FCSTD DOCUMENT  (FreeCAD 1.0R38641 +678 (Git))
Label: Disco_assembly
License: All rights reserved
LicenseURL: https://en.wikipedia.org/wiki/All_rights_reserved
objects: App::Link×6, App::FeaturePython×5, Assembly::JointGroup×1, Assembly::AssemblyObject×1
EXTERNAL_REF file=Disco_base.FCStd obj=Body
EXTERNAL_REF file=Disco_base.FCStd obj=Body001
EXTERNAL_REF file=Disco_deck.FCStd obj=Body001
EXTERNAL_REF file=Disco_motor-spool.FCStd obj=Body
EXTERNAL_REF file=Disco_ball.FCStd obj=Body

FEATURE [App::Link] ColorLEDdeck
  LinkedObject = -> <external Disco_base.FCStd>#Body
FEATURE [App::FeaturePython] GroundedJoint  # Assembly grounded joint (typed FeaturePython)
  ObjectToGround = -> ColorLEDdeck
FEATURE [App::Link] Body
  LinkPlacement = pos=(-5e-16,0,0) rot=(0,0,1;0rad)
  LinkedObject = -> <external Disco_base.FCStd>#Body001
  Placement = pos=(-5e-16,0,0) rot=(0,0,1;0rad)
FEATURE [App::Link] Body001
  LinkPlacement = pos=(0,0,0) rot=(0,0,1;3.14159rad)
  LinkedObject = -> <external Disco_base.FCStd>#Body001
  Placement = pos=(0,0,0) rot=(0,0,1;3.14159rad)
FEATURE [App::Link] Body002
  LinkPlacement = pos=(-0.0296618,0.020308,-2.57969) rot=(0.57735,0.57735,-0.57735;2.0944rad)
  LinkedObject = -> <external Disco_deck.FCStd>#Body001
  Placement = pos=(-0.0296618,0.020308,-2.57969) rot=(0.57735,0.57735,-0.57735;2.0944rad)
FEATURE [App::Link] Body003
  LinkPlacement = pos=(-0.0413632,-24.6067,1.66004) rot=(0,0,1;0rad)
  LinkedObject = -> <external Disco_motor-spool.FCStd>#Body
  Placement = pos=(-0.0413632,-24.6067,1.66004) rot=(0,0,1;0rad)
FEATURE [App::Link] Body004
  LinkPlacement = pos=(-1.4e-15,-1.316e-13,8.9e-15) rot=(0,0,1;3.14159rad)
  LinkedObject = -> <external Disco_ball.FCStd>#Body
  Placement = pos=(-1.4e-15,-1.316e-13,8.9e-15) rot=(0,0,1;3.14159rad)
FEATURE [App::FeaturePython] Joint  label="Distance"  # Assembly joint (typed FeaturePython)
  Activated = true
  AngleMax = 0
  AngleMin = 0
  Detach1 = false
  Detach2 = false
  Distance = 0
  Distance2 = 0
  EnableAngleMax = false
  EnableAngleMin = false
  EnableLengthMax = false
  EnableLengthMin = false
  JointType = 5 (Distance)
  LengthMax = 0
  LengthMin = 0
  Placement1 = pos=(-14.2217,-1.5e-15,0) rot=(0,1,0;3.14159rad)
  Placement2 = pos=(-1.1e-15,-1.43e-13,0) rot=(0,0,1;0rad)
  Reference1 = -> Assembly [Body.Hole.Face2,Body.Hole.Face2]
  Reference2 = -> Assembly [ColorLEDdeck.Pad.Face11,ColorLEDdeck.Pad.Face11]
FEATURE [App::FeaturePython] Joint001  label="Fixed"  # Assembly joint (typed FeaturePython)
  Activated = true
  AngleMax = 0
  AngleMin = 0
  Detach1 = false
  Detach2 = false
  Distance = 0
  Distance2 = 0
  EnableAngleMax = false
  EnableAngleMin = false
  EnableLengthMax = false
  EnableLengthMin = false
  JointType = 0 (Fixed)
  LengthMax = 0
  LengthMin = 0
  Placement1 = pos=(-15,0,0) rot=(0,1,0;3.14159rad)
  Placement2 = pos=(-15,0,0) rot=(0,0,1;0rad)
  Reference1 = -> Assembly [Body.Hole.Edge14,Body.Hole.Edge14]
  Reference2 = -> Assembly [ColorLEDdeck.Pad.Edge29,ColorLEDdeck.Pad.Edge29]
FEATURE [App::FeaturePython] Joint002  label="Fixed001"  # Assembly joint (typed FeaturePython)
  Activated = true
  AngleMax = 0
  AngleMin = 0
  Detach1 = false
  Detach2 = false
  Distance = 0
  Distance2 = 0
  EnableAngleMax = false
  EnableAngleMin = false
  EnableLengthMax = false
  EnableLengthMin = false
  JointType = 0 (Fixed)
  LengthMax = 0
  LengthMin = 0
  Placement1 = pos=(-15,0,0) rot=(0,-1,0;3.14159rad)
  Placement2 = pos=(15,0,0) rot=(0,0,1;0rad)
  Reference1 = -> Assembly [Body001.Hole.Edge14,Body001.Hole.Edge14]
  Reference2 = -> Assembly [ColorLEDdeck.Pad.Edge26,ColorLEDdeck.Pad.Edge26]
FEATURE [App::FeaturePython] Joint003  label="Distance001"  # Assembly joint (typed FeaturePython)
  Activated = true
  AngleMax = 0
  AngleMin = 0
  Detach1 = false
  Detach2 = false
  Distance = 0
  Distance2 = 0
  EnableAngleMax = false
  EnableAngleMin = false
  EnableLengthMax = false
  EnableLengthMin = false
  JointType = 5 (Distance)
  LengthMax = 0
  LengthMin = 0
  Placement1 = pos=(9.4e-15,1.08e-14,-8.9e-15) rot=(0,0,-1;3.14159rad)
  Placement2 = pos=(-1.1e-15,-1.43e-13,0) rot=(0,0,1;0rad)
  Reference1 = -> Assembly [Body004.Cylinder003.Face33,Body004.Cylinder003.Face33]
  Reference2 = -> Assembly [ColorLEDdeck.Pad.Face11,ColorLEDdeck.Pad.Face11]
FEATURE [Assembly::JointGroup] Joints
  Group = -> [GroundedJoint,Joint,Joint001,Joint002,Joint003]
FEATURE [Assembly::AssemblyObject] Assembly
  Group = -> [Joints,ColorLEDdeck,GroundedJoint,Body,Body001,Body002,Body003,Body004,Joint,Joint001,Joint002,Joint003]
  Origin = -> Origin
  Type = Assembly

RESOLVED EXTERNAL PARTS (link-assembly join: the EXTERNAL_REF files above that resolve inside this repo's crawl, each included once):
---- part Disco_ball.FCStd = doc fcstd_ed00773c9699 ----
FCSTD DOCUMENT  (FreeCAD 1.0R38641 +678 (Git))
Label: Disco_ball
License: All rights reserved
LicenseURL: https://en.wikipedia.org/wiki/All_rights_reserved
objects: PartDesign::PolarPattern×4, PartDesign::SubtractiveCylinder×4, Sketcher::SketchObject×2, PartDesign::Revolution×1, PartDesign::Plane×1, PartDesign::Pocket×1, PartDesign::Body×1
note: 32 computed .brp shape members not serialized (recipe doc carries the construction recipe); baked Part::Feature solids carry a one-line shape summary decoded from their .brp

FEATURE [Sketcher::SketchObject] Sketch
  ArcFitTolerance = 1e-06
  AttachmentSupport = -> [XZ_Plane]
  FullyConstrained = true
  MakeInternals = false
  MapMode = 5
  Placement = pos=(0,0,0) rot=(1,0,0;1.5708rad)
  sketch-geometry (15):
    g0: LineSegment [constr] StartX=-16.6 StartY=0 StartZ=0 EndX=-16.6 EndY=-0.8 EndZ=0
    g1: LineSegment [constr] StartX=-16.6 StartY=-0.8 StartZ=0 EndX=16.6 EndY=-0.8 EndZ=0
    g2: LineSegment [constr] StartX=16.6 StartY=-0.8 StartZ=0 EndX=16.6 EndY=0 EndZ=0
    g3: LineSegment [constr] StartX=16.6 StartY=0 StartZ=0 EndX=-16.6 EndY=0 EndZ=0
    g4: ArcOfCircle CenterX=0 CenterY=15 CenterZ=0 NormalX=0 NormalY=0 NormalZ=1 AngleXU=0 Radius=16 StartAngle=5.3481 EndAngle=7.85398
    g5: ArcOfCircle CenterX=0 CenterY=15 CenterZ=0 NormalX=0 NormalY=0 NormalZ=1 AngleXU=0 Radius=17 StartAngle=5.54023 EndAngle=7.85398
    g6: LineSegment StartX=0 StartY=32 StartZ=0 EndX=4.9e-15 EndY=31 EndZ=0
    g7: LineSegment StartX=11.7 StartY=1.45 StartZ=0 EndX=13.5 EndY=1.45 EndZ=0
    g8: LineSegment StartX=9.5 StartY=2.12561 StartZ=0 EndX=9.5 EndY=0 EndZ=0
    g9: LineSegment StartX=9.5 StartY=0 StartZ=0 EndX=13.5 EndY=0 EndZ=0
    g10: LineSegment StartX=13.5 StartY=0 StartZ=0 EndX=13.5 EndY=1.45 EndZ=0
    g11: ArcOfCircle CenterX=11.7 CenterY=1.75 CenterZ=0 NormalX=0 NormalY=0 NormalZ=1 AngleXU=0 Radius=0.3 StartAngle=2.08659 EndAngle=4.71239
    g12: LineSegment StartX=12.52 StartY=3.5 StartZ=0 EndX=13.42 EndY=3.5 EndZ=0
    g13: LineSegment StartX=11.552 StartY=2.01097 StartZ=0 EndX=13.5186 EndY=3.12602 EndZ=0
    g14: ArcOfCircle CenterX=13.42 CenterY=3.3 CenterZ=0 NormalX=0 NormalY=0 NormalZ=1 AngleXU=0 Radius=0.2 StartAngle=5.22819 EndAngle=7.85398
  constraints (43):
    c: Coincident(g0,g1)
    c: Coincident(g1,g2)
    c: Coincident(g2,g3)
    c: Coincident(g3,g0)
    c: Vertical(g0)
    c: Vertical(g2)
    c: Horizontal(g1)
    c: Symmetric(g2,g0,g-2)
    c: PointOnObject(g0,g-1)
    c: Distance(g1,g1) = 33.2
    c: Distance(g0,g0) = 0.8
    c: PointOnObject(g4,g-2)
    c: Diameter(g4) = 32
    c: DistanceY(g-1,g4) = 15
    c: PointOnObject(g4,g-2)
    c: Coincident(g5,g4)
    c: PointOnObject(g5,g-2)
    c: Coincident(g6,g5)
    c: Coincident(g6,g4)
    c: Horizontal(g7)
    c: Distance(g9,g7) = 1.45
    c: Coincident(g8,g4)
    c: PointOnObject(g8,g3)
    c: Coincident(g9,g8)
    c: Vertical(g8)
    c: Coincident(g10,g9)
    c: Coincident(g10,g7)
    c: Vertical(g10)
    c: PointOnObject(g9,g-1)
    c: DistanceX(g-1,g9) = 13.5
    c: Diameter(g11) = 0.6
    c: Distance(g4,g5) = 1
    c: Tangent(g11,g7) = -1.5708
    c: DistanceX(g9,g9) = 4
    c: Horizontal(g12)
    c: Coincident(g5,g12)
    c: Tangent(g13,g11) = 1.5708
    c: DistanceX(g7,g7) = 1.8
    c: Diameter(g14) = 0.4
    c: Distance(g12,g12) = 0.9
    c: DistanceY(g-1,g12) = 3.5
    c: Tangent(g14,g12) = 1.5708
    c: Tangent(g14,g13) = -1.5708
FEATURE [PartDesign::Revolution] Revolution
  Angle = 360
  Angle2 = 60
  Axis = (0,2e-16,1)
  Base = (0,0,0)
  Placement = pos=(0,0,0) rot=(1,0,0;1.5708rad)
  Profile = -> Sketch
  ReferenceAxis = -> Sketch [V_Axis]
  Refine = true
  Reversed = true
  Suppressed = false
  Type = 0
FEATURE [PartDesign::Plane] DatumPlane
  AttachmentOffset = pos=(19,0,0) rot=(0,1,0;1.5708rad)
  AttachmentSupport = -> [Revolution]
  Length = 60
  MapMode = 45
  Placement = pos=(19,4.9e-15,17.75) rot=(0,1,0;1.5708rad)
  ResizeMode = 0
  Width = 60
FEATURE [Sketcher::SketchObject] Sketch001
  ArcFitTolerance = 1e-06
  AttachmentSupport = -> [DatumPlane]
  FullyConstrained = true
  MakeInternals = false
  MapMode = 5
  Placement = pos=(19,4.9e-15,17.75) rot=(0,1,0;1.5708rad)
  sketch-geometry (1):
    g0: Circle CenterX=0 CenterY=0 CenterZ=0 NormalX=0 NormalY=0 NormalZ=1 AngleXU=0 Radius=3
  constraints (2):
    c: Coincident(g0,g-1)
    c: Diameter(g0) = 6
FEATURE [PartDesign::Pocket] Pocket
  BaseFeature = -> Revolution
  Direction = (-1,0,-2e-16)
  Length = 7
  Length2 = 5
  Placement = pos=(0,0,0) rot=(1,0,0;1.5708rad)
  Profile = -> Sketch001
  ReferenceAxis = -> Sketch001 [N_Axis]
  Refine = true
  Suppressed = false
  Type = 0
FEATURE [PartDesign::PolarPattern] PolarPattern
  Angle = 360
  Axis = -> Z_Axis
  BaseFeature = -> Pocket
  Mode = 0
  Occurrences = 8
  Offset = 120
  Originals = -> [Pocket]
  Placement = pos=(0,0,0) rot=(1,0,0;1.5708rad)
  Refine = true
  Suppressed = false
  TransformMode = 0
FEATURE [PartDesign::SubtractiveCylinder] Cylinder
  Angle = 360
  AttacherType = Attacher::AttachEngine3D
  AttachmentOffset = pos=(0,17.7,0) rot=(-0.799605,-0.580063,-0.155428;0.646683rad)
  AttachmentSupport = -> [YZ_Plane]
  BaseFeature = -> PolarPattern
  FirstAngle = 0
  Height = 21
  MapMode = 5
  Placement = pos=(0,0,17.7) rot=(0.595507,0.401675,0.695721;1.53984rad)
  Radius = 3
  Refine = true
  SecondAngle = 0
  Suppressed = false
FEATURE [PartDesign::PolarPattern] PolarPattern001
  Angle = 360
  Axis = -> Z_Axis
  BaseFeature = -> Cylinder
  Mode = 0
  Occurrences = 8
  Offset = 120
  Originals = -> [Cylinder]
  Placement = pos=(0,0,17.7) rot=(0.595507,0.401675,0.695721;1.53984rad)
  Refine = true
  Suppressed = false
  TransformMode = 0
FEATURE [PartDesign::SubtractiveCylinder] Cylinder001
  Angle = 360
  AttacherType = Attacher::AttachEngine3D
  AttachmentOffset = pos=(0,17.7,0) rot=(-1,0,0;1.0472rad)
  AttachmentSupport = -> [XZ_Plane]
  BaseFeature = -> PolarPattern001
  FirstAngle = 0
  Height = 25
  MapMode = 5
  Placement = pos=(0,3.9e-15,17.7) rot=(1,0,0;0.523599rad)
  Radius = 3
  Refine = true
  SecondAngle = 0
  Suppressed = false
FEATURE [PartDesign::PolarPattern] PolarPattern002
  Angle = 360
  Axis = -> Z_Axis
  BaseFeature = -> Cylinder001
  Mode = 0
  Occurrences = 4
  Offset = 120
  Originals = -> [Cylinder001]
  Placement = pos=(0,3.9e-15,17.7) rot=(1,0,0;0.523599rad)
  Refine = true
  Suppressed = false
  TransformMode = 0
FEATURE [PartDesign::SubtractiveCylinder] Cylinder002
  Angle = 360
  AttacherType = Attacher::AttachEngine3D
  AttachmentOffset = pos=(0,17.7,0) rot=(0.744004,-0.652337,0.14462;0.579196rad)
  AttachmentSupport = -> [XZ_Plane]
  BaseFeature = -> PolarPattern002
  FirstAngle = 0
  Height = 37
  MapMode = 5
  Placement = pos=(0,3.9e-15,17.7) rot=(0.974454,-0.189415,-0.12067;2.03045rad)
  Radius = 3
  Refine = true
  SecondAngle = 0
  Suppressed = false
FEATURE [PartDesign::PolarPattern] PolarPattern003
  Angle = 360
  Axis = -> Z_Axis
  BaseFeature = -> Cylinder002
  Mode = 0
  Occurrences = 8
  Offset = 120
  Originals = -> [Cylinder002]
  Placement = pos=(0,3.9e-15,17.7) rot=(0.974454,-0.189415,-0.12067;2.03045rad)
  Refine = true
  Suppressed = false
  TransformMode = 0
FEATURE [PartDesign::SubtractiveCylinder] Cylinder003
  Angle = 360
  AttacherType = Attacher::AttachEngine3D
  AttachmentSupport = -> [XY_Plane]
  BaseFeature = -> PolarPattern003
  FirstAngle = 0
  Height = 46
  MapMode = 5
  Radius = 3
  Refine = true
  SecondAngle = 0
  Suppressed = false
FEATURE [PartDesign::Body] Body
  AllowCompound = false
  Group = -> [Sketch,Revolution,DatumPlane,Sketch001,Pocket,PolarPattern,Cylinder,PolarPattern001,Cylinder001,PolarPattern002,Cylinder002,PolarPattern003,Cylinder003]
  Origin = -> Origin
  Tip = -> Cylinder003
---- part Disco_base.FCStd = doc fcstd_412642338aae ----
FCSTD DOCUMENT  (FreeCAD 1.0R38641 +678 (Git))
Label: Disco_base
License: All rights reserved
LicenseURL: https://en.wikipedia.org/wiki/All_rights_reserved
objects: Sketcher::SketchObject×5, PartDesign::Pad×4, PartDesign::Mirrored×3, PartDesign::Body×2, PartDesign::Hole×1
note: 33 computed .brp shape members not serialized (recipe doc carries the construction recipe); baked Part::Feature solids carry a one-line shape summary decoded from their .brp

FEATURE [Sketcher::SketchObject] Sketch
  ArcFitTolerance = 1e-06
  AttachmentSupport = -> [XY_Plane]
  FullyConstrained = true
  MakeInternals = false
  MapMode = 5
  sketch-geometry (10):
    g0: ArcOfCircle CenterX=0 CenterY=0 CenterZ=0 NormalX=0 NormalY=0 NormalZ=1 AngleXU=0 Radius=16.6347 StartAngle=3.37071 EndAngle=4.48327
    g1: LineSegment StartX=-3.77799 StartY=16.2 StartZ=0 EndX=3.77799 EndY=16.2 EndZ=0
    g2: LineSegment StartX=-3.77799 StartY=-16.2 StartZ=0 EndX=3.77799 EndY=-16.2 EndZ=0
    g3: LineSegment StartX=-16.2 StartY=3.77799 StartZ=0 EndX=-16.2 EndY=-3.77799 EndZ=0
    g4: LineSegment StartX=16.2 StartY=3.77799 StartZ=0 EndX=16.2 EndY=-3.77799 EndZ=0
    g5: ArcOfCircle CenterX=0 CenterY=0 CenterZ=0 NormalX=0 NormalY=0 NormalZ=1 AngleXU=0 Radius=16.6347 StartAngle=0.229115 EndAngle=1.34168
    g6: ArcOfCircle CenterX=0 CenterY=0 CenterZ=0 NormalX=0 NormalY=0 NormalZ=1 AngleXU=0 Radius=16.6347 StartAngle=4.9415 EndAngle=6.05407
    g7: ArcOfCircle CenterX=0 CenterY=0 CenterZ=0 NormalX=0 NormalY=0 NormalZ=1 AngleXU=0 Radius=16.6347 StartAngle=1.79991 EndAngle=2.91248
    g8: Circle CenterX=-15 CenterY=0 CenterZ=0 NormalX=0 NormalY=0 NormalZ=1 AngleXU=0 Radius=0.86
    g9: Circle CenterX=15 CenterY=0 CenterZ=0 NormalX=0 NormalY=0 NormalZ=1 AngleXU=0 Radius=0.86
  constraints (32):
    c: Coincident(g0,g-1)
    c: Radius(g0) = 16.6347
    c: PointOnObject(g1,g7)
    c: Horizontal(g1)
    c: PointOnObject(g2,g6)
    c: Horizontal(g2)
    c: Symmetric(g1,g2,g-1)
    c: Distance(g2,g1) = 32.4
    c: Vertical(g3)
    c: PointOnObject(g4,g5)
    c: Vertical(g4)
    c: Symmetric(g3,g4,g-2)
    c: Distance(g4,g3) = 32.4
    c: Coincident(g7,g3)
    c: Coincident(g0,g3)
    c: Equal(g0,g5)
    c: PointOnObject(g6,g4)
    c: PointOnObject(g5,g4)
    c: Coincident(g0,g5)
    c: Equal(g0,g6)
    c: PointOnObject(g0,g2)
    c: PointOnObject(g6,g2)
    c: Coincident(g0,g6)
    c: Equal(g5,g7)
    c: Coincident(g5,g1)
    c: PointOnObject(g7,g1)
    c: Coincident(g5,g7)
    c: PointOnObject(g8,g-1)
    c: Diameter(g8) = 1.72
    c: Diameter(g9) = 1.72
    c: Symmetric(g8,g9,g-2)
    c: DistanceX(g8,g9) = 30
FEATURE [PartDesign::Pad] Pad
  Direction = (0,0,1)
  Length = 0.8
  Length2 = 10
  Profile = -> Sketch
  ReferenceAxis = -> Sketch [N_Axis]
  Refine = true
  Reversed = true
  Suppressed = false
  Type = 0
FEATURE [PartDesign::Body] Body  label="ColorLEDdeck"
  AllowCompound = false
  Group = -> [Sketch,Pad]
  Origin = -> Origin
  Tip = -> Pad
FEATURE [Sketcher::SketchObject] Sketch001
  ArcFitTolerance = 1e-06
  AttachmentSupport = -> [XY_Plane001]
  FullyConstrained = true
  MakeInternals = false
  MapMode = 5
  sketch-geometry (4):
    g0: ArcOfCircle CenterX=0 CenterY=0 CenterZ=0 NormalX=0 NormalY=0 NormalZ=1 AngleXU=0 Radius=13.6347 StartAngle=2.53073 EndAngle=3.14159
    g1: ArcOfCircle CenterX=0 CenterY=0 CenterZ=0 NormalX=0 NormalY=0 NormalZ=1 AngleXU=0 Radius=16.6347 StartAngle=2.53073 EndAngle=3.14159
    g2: LineSegment StartX=-16.6347 StartY=0 StartZ=0 EndX=-13.6347 EndY=1.7e-15 EndZ=0
    g3: LineSegment StartX=-13.6263 StartY=9.54127 StartZ=0 EndX=-11.1689 EndY=7.82054 EndZ=0
  constraints (12):
    c: Coincident(g0,g-1)
    c: Radius(g1) = 16.6347
    c: Coincident(g1,g0)
    c: PointOnObject(g1,g-1)
    c: PointOnObject(g0,g-1)
    c: Distance(g1,g0) = 3
    c: Coincident(g2,g1)
    c: Coincident(g2,g0)
    c: Coincident(g3,g1)
    c: Coincident(g3,g0)
    c: Perpendicular(g0,g3)
    c: Angle(g0) = 0.610865
FEATURE [PartDesign::Pad] Pad001
  Direction = (0,0,1)
  Length = 1.5
  Length2 = 10
  Profile = -> Sketch001
  ReferenceAxis = -> Sketch001 [N_Axis]
  Refine = true
  Suppressed = false
  Type = 0
FEATURE [PartDesign::Mirrored] Mirrored
  BaseFeature = -> Pad001
  MirrorPlane = -> XZ_Plane001
  Originals = -> [Pad001]
  Refine = true
  Suppressed = false
  TransformMode = 0
FEATURE [Sketcher::SketchObject] Sketch002
  ArcFitTolerance = 1e-06
  AttachmentSupport = -> [Mirrored]
  ExternalGeometry = -> [Mirrored]
  FullyConstrained = true
  MakeInternals = false
  MapMode = 5
  Placement = pos=(0,0,1.5) rot=(0,0,1;0rad)
  sketch-geometry (4):
    g0: ArcOfCircle CenterX=0 CenterY=0 CenterZ=0 NormalX=0 NormalY=0 NormalZ=1 AngleXU=0 Radius=16.6347 StartAngle=2.53073 EndAngle=3.14159
    g1: LineSegment StartX=-13.6263 StartY=9.54127 StartZ=0 EndX=-10.3497 EndY=7.24697 EndZ=0
    g2: ArcOfCircle CenterX=0 CenterY=0 CenterZ=0 NormalX=0 NormalY=0 NormalZ=1 AngleXU=0 Radius=12.6347 StartAngle=2.53073 EndAngle=3.14159
    g3: LineSegment StartX=-16.6347 StartY=1.5e-15 StartZ=0 EndX=-12.6347 EndY=1.5e-15 EndZ=0
  constraints (11):
    c: Coincident(g0,g-1)
    c: Coincident(g0,g-3)
    c: Coincident(g1,g0)
    c: Perpendicular(g0,g1)
    c: Distance(g1,g1) = 4
    c: Coincident(g2,g0)
    c: Coincident(g2,g1)
    c: PointOnObject(g2,g-1)
    c: Coincident(g3,g0)
    c: Coincident(g3,g2)
    c: Horizontal(g3)
FEATURE [PartDesign::Pad] Pad002
  BaseFeature = -> Mirrored
  Direction = (0,0,1)
  Length = 1
  Length2 = 10
  Profile = -> Sketch002
  ReferenceAxis = -> Sketch002 [N_Axis]
  Refine = true
  Suppressed = false
  Type = 0
FEATURE [PartDesign::Mirrored] Mirrored001
  BaseFeature = -> Pad002
  MirrorPlane = -> XZ_Plane001
  Originals = -> [Pad002]
  Refine = true
  Suppressed = false
  TransformMode = 0
FEATURE [Sketcher::SketchObject] Sketch003
  ArcFitTolerance = 1e-06
  AttachmentSupport = -> [Mirrored001]
  ExternalGeometry = -> [Mirrored001]
  FullyConstrained = true
  MakeInternals = false
  MapMode = 5
  Placement = pos=(0,0,0) rot=(1,0,0;3.14159rad)
  sketch-geometry (4):
    g0: ArcOfCircle CenterX=0 CenterY=0 CenterZ=0 NormalX=0 NormalY=0 NormalZ=1 AngleXU=0 Radius=18.1347 StartAngle=2.53073 EndAngle=3.14159
    g1: ArcOfCircle CenterX=0 CenterY=0 CenterZ=0 NormalX=0 NormalY=0 NormalZ=1 AngleXU=0 Radius=16.6347 StartAngle=2.53073 EndAngle=3.14159
    g2: LineSegment StartX=-18.1347 StartY=2e-15 StartZ=0 EndX=-16.6347 EndY=2e-15 EndZ=0
    g3: LineSegment StartX=-14.8551 StartY=10.4016 StartZ=0 EndX=-13.6263 EndY=9.54127 EndZ=0
  constraints (11):
    c: Coincident(g0,g-1)
    c: PointOnObject(g0,g-1)
    c: Coincident(g1,g0)
    c: Coincident(g1,g-3)
    c: Coincident(g2,g0)
    c: Coincident(g2,g1)
    c: Horizontal(g2)
    c: Coincident(g3,g0)
    c: Coincident(g3,g1)
    c: DistanceX(g2,g2) = 1.5
    c: Perpendicular(g1,g3)
FEATURE [PartDesign::Pad] Pad003
  BaseFeature = -> Mirrored001
  Direction = (0,0,-1)
  Length = 0.8
  Length2 = 2.5
  Profile = -> Sketch003
  ReferenceAxis = -> Sketch003 [N_Axis]
  Refine = true
  Suppressed = false
  Type = 4
FEATURE [PartDesign::Mirrored] Mirrored002
  BaseFeature = -> Pad003
  MirrorPlane = -> XZ_Plane001
  Originals = -> [Pad003]
  Refine = true
  Suppressed = false
  TransformMode = 0
FEATURE [Sketcher::SketchObject] Sketch004
  ArcFitTolerance = 1e-06
  AttachmentSupport = -> [Mirrored002]
  FullyConstrained = true
  MakeInternals = false
  MapMode = 5
  Placement = pos=(0,0,0) rot=(1,0,0;3.14159rad)
  sketch-geometry (1):
    g0: Circle CenterX=-15 CenterY=0 CenterZ=0 NormalX=0 NormalY=0 NormalZ=1 AngleXU=0 Radius=0.5
  constraints (3):
    c: PointOnObject(g0,g-1)
    c: DistanceX(g0,g-1) = 15
    c: Diameter(g0) = 1
FEATURE [PartDesign::Hole] Hole
  BaseFeature = -> Mirrored002
  CustomThreadClearance = 0
  Depth = 25
  DepthType = 0
  Diameter = 1.8
  DrillForDepth = false
  DrillPoint = 0
  DrillPointAngle = 118
  HoleCutCountersinkAngle = 90
  HoleCutCustomValues = false
  HoleCutDepth = 0
  HoleCutDiameter = 6.1
  HoleCutType = 0
  ModelThread = false
  Profile = -> Sketch004
  Refine = true
  Suppressed = false
  Tapered = false
  TaperedAngle = 90
  ThreadClass = 0
  ThreadDepth = 25
  ThreadDepthType = 0
  ThreadDirection = 0
  ThreadFit = 0
  ThreadSize = 4
  ThreadType = 1
  Threaded = false
  UseCustomThreadClearance = false
FEATURE [PartDesign::Body] Body001  label="Body"
  AllowCompound = false
  Group = -> [Sketch001,Pad001,Mirrored,Sketch002,Pad002,Mirrored001,Sketch003,Pad003,Mirrored002,Sketch004,Hole]
  Origin = -> Origin001
  Tip = -> Hole
---- part Disco_deck.FCStd = doc fcstd_9cf34fc2a8e8 ----
FCSTD DOCUMENT  (FreeCAD 1.0R38641 +678 (Git))
Label: Disco_deck
License: All rights reserved
LicenseURL: https://en.wikipedia.org/wiki/All_rights_reserved
objects: Sketcher::SketchObject×2, PartDesign::Pad×2, PartDesign::Fillet×2, PartDesign::Mirrored×1, PartDesign::Body×1
note: 19 computed .brp shape members not serialized (recipe doc carries the construction recipe); baked Part::Feature solids carry a one-line shape summary decoded from their .brp

FEATURE [Sketcher::SketchObject] Sketch001
  ArcFitTolerance = 1e-06
  AttachmentSupport = -> [YZ_Plane001]
  FullyConstrained = true
  MakeInternals = false
  MapMode = 5
  Placement = pos=(0,0,0) rot=(0.57735,0.57735,0.57735;2.0944rad)
  sketch-geometry (14):
    g0: LineSegment StartX=-13 StartY=10.5 StartZ=0 EndX=-13 EndY=-10.5 EndZ=0
    g1: LineSegment StartX=-13 StartY=-10.5 StartZ=0 EndX=0 EndY=-10.5 EndZ=0
    g2: LineSegment StartX=-5 StartY=10.5 StartZ=0 EndX=-13 EndY=10.5 EndZ=0
    g3: LineSegment StartX=-11.3 StartY=9.25 StartZ=0 EndX=-11.3 EndY=-9.25 EndZ=0
    g4: LineSegment StartX=-11.3 StartY=-9.25 StartZ=0 EndX=-10.7 EndY=-9.25 EndZ=0
    g5: LineSegment StartX=-10.7 StartY=-9.25 StartZ=0 EndX=-10.7 EndY=9.25 EndZ=0
    g6: LineSegment StartX=-10.7 StartY=9.25 StartZ=0 EndX=-11.3 EndY=9.25 EndZ=0
    g7: LineSegment StartX=0 StartY=7.5 StartZ=0 EndX=-7 EndY=7.5 EndZ=0
    g8: LineSegment StartX=-7 StartY=7.5 StartZ=0 EndX=-7 EndY=-7.5 EndZ=0
    g9: LineSegment StartX=-7 StartY=-7.5 StartZ=0 EndX=0 EndY=-7.5 EndZ=0
    g10: LineSegment StartX=-5 StartY=10.5 StartZ=0 EndX=-2.5 EndY=21.5 EndZ=0
    g11: LineSegment StartX=0 StartY=-7.5 StartZ=0 EndX=0 EndY=-10.5 EndZ=0
    g12: LineSegment StartX=-2.5 StartY=21.5 StartZ=0 EndX=0 EndY=21.5 EndZ=0
    g13: LineSegment StartX=0 StartY=7.5 StartZ=0 EndX=0 EndY=21.5 EndZ=0
  constraints (39):
    c: Coincident(g0,g1)
    c: Coincident(g2,g0)
    c: Horizontal(g1)
    c: DistanceX(g1,g1) = 13
    c: DistanceY(g0,g0) = 21
    c: Coincident(g3,g4)
    c: Coincident(g4,g5)
    c: Coincident(g5,g6)
    c: Coincident(g6,g3)
    c: Horizontal(g4)
    c: Horizontal(g6)
    c: Horizontal(g2)
    c: Distance(g6,g6) = 0.6
    c: DistanceY(g3,g3) = 18.5
    c: DistanceX(g5,g-1) = 10.7
    c: Symmetric(g0,g0,g-1)
    c: Symmetric(g3,g3,g-1)
    c: Vertical(g5)
    c: Coincident(g7,g8)
    c: Coincident(g8,g9)
    c: Horizontal(g7)
    c: Horizontal(g9)
    c: Symmetric(g7,g8,g-1)
    c: DistanceX(g9,g9) = 7
    c: DistanceY(g8,g8) = 15
    c: PointOnObject(g7,g-2)
    c: DistanceY(g0,g10) = 11
    c: Coincident(g2,g10)
    c: Distance(g2,g0) = 8
    c: Coincident(g11,g9)
    c: Coincident(g11,g1)
    c: PointOnObject(g1,g-2)
    c: PointOnObject(g9,g-2)
    c: Coincident(g12,g10)
    c: PointOnObject(g12,g-2)
    c: Horizontal(g12)
    c: Distance(g12,g12) = 2.5
    c: Coincident(g13,g7)
    c: Coincident(g13,g12)
FEATURE [PartDesign::Pad] Pad001
  Direction = (1,0,0)
  Length = 3
  Length2 = 10
  Placement = pos=(0,0,0) rot=(1,1,1;2.0944rad)
  Profile = -> Sketch001
  ReferenceAxis = -> Sketch001 [N_Axis]
  Refine = true
  Suppressed = false
  Type = 0
FEATURE [Sketcher::SketchObject] Sketch002
  ArcFitTolerance = 1e-06
  AttachmentSupport = -> [Pad001]
  ExternalGeometry = -> [Pad001]
  FullyConstrained = true
  MakeInternals = false
  MapMode = 5
  Placement = pos=(3,0,0) rot=(0.57735,0.57735,0.57735;2.0944rad)
  sketch-geometry (4):
    g0: ArcOfCircle CenterX=0 CenterY=24.6225 CenterZ=0 NormalX=0 NormalY=0 NormalZ=1 AngleXU=0 Radius=3 StartAngle=2.53073 EndAngle=4.71239
    g1: ArcOfCircle CenterX=0 CenterY=24.6225 CenterZ=0 NormalX=0 NormalY=0 NormalZ=1 AngleXU=0 Radius=4 StartAngle=2.53073 EndAngle=4.71239
    g2: LineSegment StartX=-2.45746 StartY=26.3432 StartZ=0 EndX=-3.27661 EndY=26.9168 EndZ=0
    g3: LineSegment StartX=-7e-16 StartY=21.6225 StartZ=0 EndX=-7e-16 EndY=20.6225 EndZ=0
  constraints (12):
    c: PointOnObject(g0,g-2)
    c: Diameter(g1) = 8
    c: Coincident(g1,g0)
    c: Diameter(g0) = 6
    c: PointOnObject(g-3,g1)
    c: Vertical(g3)
    c: PointOnObject(g3,g-2)
    c: Angle(g2,g-3) = 0.610865
    c: Coincident(g1,g3)
    c: Coincident(g1,g2)
    c: Coincident(g0,g3)
    c: Perpendicular(g0,g2) = 4.71239
FEATURE [PartDesign::Pad] Pad002
  BaseFeature = -> Pad001
  Direction = (1,0,0)
  Length = 9
  Length2 = 3
  Placement = pos=(0,0,0) rot=(1,1,1;2.0944rad)
  Profile = -> Sketch002
  ReferenceAxis = -> Sketch002 [N_Axis]
  Refine = true
  Suppressed = false
  Type = 4
FEATURE [PartDesign::Mirrored] Mirrored
  BaseFeature = -> Pad002
  MirrorPlane = -> XZ_Plane001
  Placement = pos=(0,0,0) rot=(1,1,1;2.0944rad)
  Refine = true
  Suppressed = false
  TransformMode = 1
FEATURE [PartDesign::Fillet] Fillet
  Base = -> Mirrored [Edge42,Edge44,Edge8,Edge5]
  BaseFeature = -> Mirrored
  Placement = pos=(0,0,0) rot=(1,1,1;2.0944rad)
  Radius = 1
  Refine = true
  SupportTransform = false
  Suppressed = false
  UseAllEdges = false
FEATURE [PartDesign::Fillet] Fillet001
  Base = -> Fillet [Edge3,Edge60]
  BaseFeature = -> Fillet
  Placement = pos=(0,0,0) rot=(1,1,1;2.0944rad)
  Radius = 2
  Refine = true
  SupportTransform = false
  Suppressed = false
  UseAllEdges = false
FEATURE [PartDesign::Body] Body001  label="Body"
  AllowCompound = false
  Group = -> [Sketch001,Pad001,Sketch002,Pad002,Mirrored,Fillet,Fillet001]
  Origin = -> Origin001
  Tip = -> Fillet001
---- part Disco_motor-spool.FCStd = doc fcstd_15cc996739a8 ----
FCSTD DOCUMENT  (FreeCAD 1.0R38641 +678 (Git))
Label: Disco_motor-spool
License: All rights reserved
LicenseURL: https://en.wikipedia.org/wiki/All_rights_reserved
objects: Sketcher::SketchObject×3, PartDesign::Pad×1, PartDesign::Pocket×1, PartDesign::SubtractiveTorus×1, PartDesign::Body×1
note: 16 computed .brp shape members not serialized (recipe doc carries the construction recipe); baked Part::Feature solids carry a one-line shape summary decoded from their .brp

FEATURE [Sketcher::SketchObject] Sketch
  ArcFitTolerance = 1e-06
  AttachmentSupport = -> [XY_Plane]
  FullyConstrained = true
  MakeInternals = false
  MapMode = 5
  expr: Constraints[5] = 1.6 - 0.975
  sketch-geometry (3):
    g0: Circle CenterX=0 CenterY=0 CenterZ=0 NormalX=0 NormalY=0 NormalZ=1 AngleXU=0 Radius=3
    g1: ArcOfCircle CenterX=0 CenterY=0 CenterZ=0 NormalX=0 NormalY=0 NormalZ=1 AngleXU=0 Radius=1.05 StartAngle=5.64562 EndAngle=10.0623
    g2: LineSegment StartX=-0.843727 StartY=-0.625 StartZ=0 EndX=0.843727 EndY=-0.625 EndZ=0
  constraints (8):
    c: Coincident(g0,g-1)
    c: Diameter(g0) = 6
    c: Diameter(g1) = 2.1
    c: Coincident(g1,g0)
    c: Horizontal(g2)
    c: Distance(g0,g2) = 0.625
    c: Coincident(g1,g2)
    c: Coincident(g1,g2)
FEATURE [PartDesign::Pad] Pad
  Direction = (0,0,1)
  Length = 3.5
  Length2 = 10
  Profile = -> Sketch
  ReferenceAxis = -> Sketch [N_Axis]
  Refine = true
  Suppressed = false
  Type = 0
FEATURE [Sketcher::SketchObject] Sketch001
  ArcFitTolerance = 1e-06
  AttachmentSupport = -> [Pad]
  FullyConstrained = true
  MakeInternals = false
  MapMode = 5
  Placement = pos=(0,0,0) rot=(1,0,0;3.14159rad)
FEATURE [Sketcher::SketchObject] Sketch002
  ArcFitTolerance = 1e-06
  AttachmentSupport = -> [Pad]
  FullyConstrained = true
  MakeInternals = false
  MapMode = 5
  Placement = pos=(0,0,0) rot=(1,0,0;3.14159rad)
  sketch-geometry (1):
    g0: Circle CenterX=0 CenterY=0 CenterZ=0 NormalX=0 NormalY=0 NormalZ=1 AngleXU=0 Radius=1.75
  constraints (2):
    c: Diameter(g0) = 3.5
    c: Coincident(g0,g-1)
FEATURE [PartDesign::Pocket] Pocket
  BaseFeature = -> Pad
  Direction = (0,0,1)
  Length = 1.2
  Length2 = 5
  Profile = -> Sketch002
  ReferenceAxis = -> Sketch002 [N_Axis]
  Refine = true
  Suppressed = false
  Type = 0
FEATURE [PartDesign::SubtractiveTorus] Torus
  Angle1 = -180
  Angle2 = 180
  Angle3 = 360
  AttacherType = Attacher::AttachEngine3D
  AttachmentOffset = pos=(0,0,1.75) rot=(0,0,1;0rad)
  AttachmentSupport = -> [XY_Plane,Origin]
  BaseFeature = -> Pocket
  Placement = pos=(0,0,1.75) rot=(0,0,1;0rad)
  Radius1 = 3.6
  Radius2 = 1
  Refine = true
  Suppressed = false
FEATURE [PartDesign::Body] Body
  AllowCompound = false
  Group = -> [Sketch,Pad,Sketch001,Sketch002,Pocket,Torus]
  Origin = -> Origin
  Tip = -> Torus
